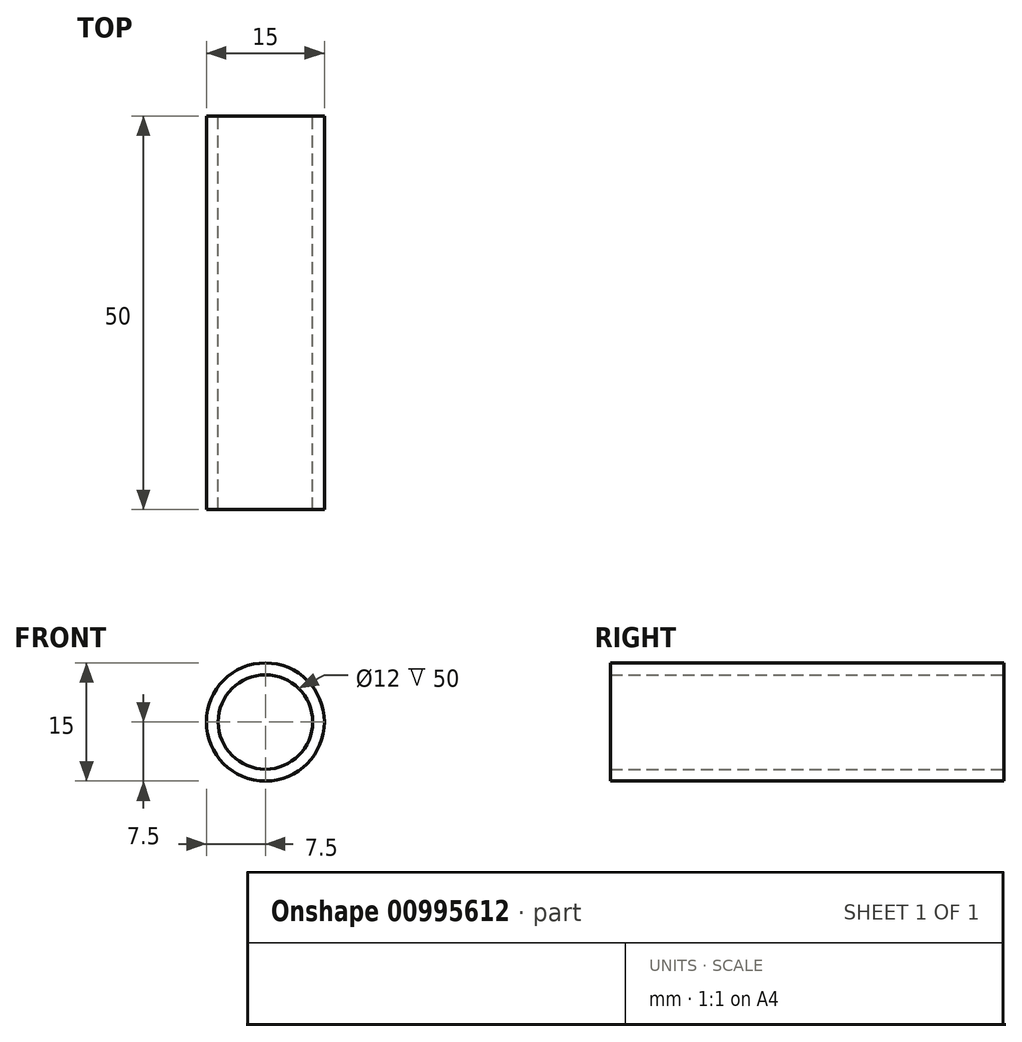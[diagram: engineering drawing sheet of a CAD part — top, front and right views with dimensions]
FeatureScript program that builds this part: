
annotation { "Feature Type Name" : "Feature", "Feature Type Description" : "" }
export const myFeature = defineFeature(function(context is Context, id is Id, definition is map)
    precondition{}
    {
        {
            var Q0;
            Q0=qCreatedBy(makeId("Front.planeOp"),FACE);
            var sketch = newSketch(context, id + "F0", { "sketchPlane" : qUnion([Q0])});
            skCircle(sketch, "E0", {"center": v(0, 0) * mm, "radius": 7.5 * mm});
            skCircle(sketch, "E1", {"center": v(0, 0) * mm, "radius": 6 * mm});
            skSolve(sketch);
        }
        {
            var Q0;
            Q0 = qSketchRegion(id + "F0", true);
            extrude(context, id + "F1", {"entities" : qUnion([Q0]), "depth" : 50 * mm, "offsetDistance" : 25 * mm});
        }
    });
